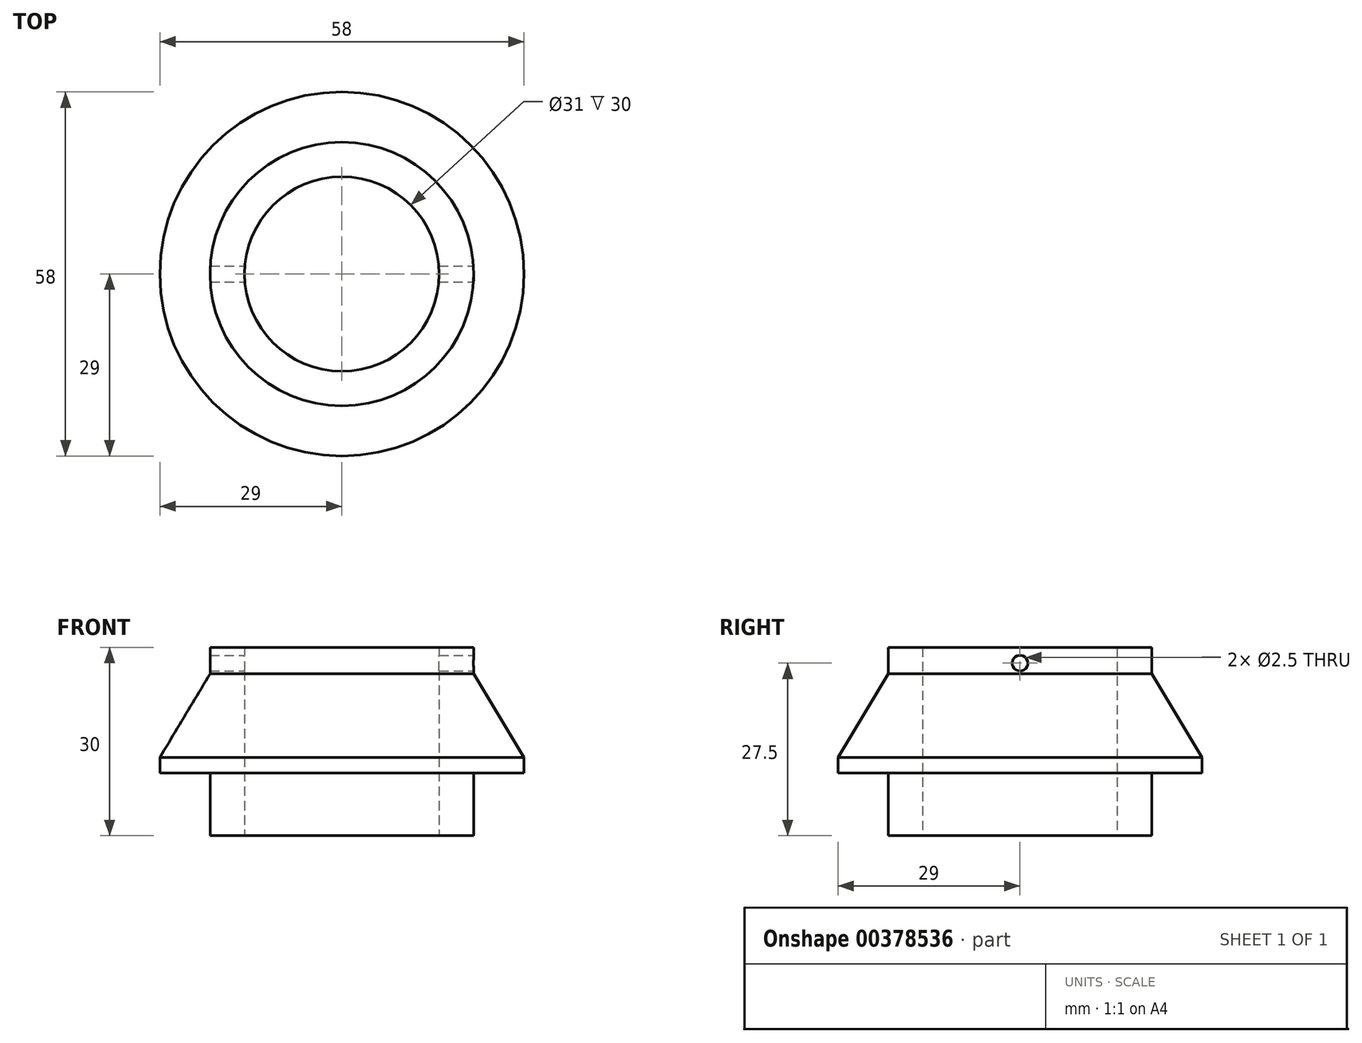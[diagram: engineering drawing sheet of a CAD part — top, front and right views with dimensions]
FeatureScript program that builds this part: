
annotation { "Feature Type Name" : "Feature", "Feature Type Description" : "" }
export const myFeature = defineFeature(function(context is Context, id is Id, definition is map)
    precondition{}
    {
        {
            var Q0;
            Q0=qCreatedBy(makeId("Front.planeOp"),FACE);
            var sketch = newSketch(context, id + "F0", { "sketchPlane" : qUnion([Q0])});
            skLineSegment(sketch, "E0.bottom", {"start": v(15.5, 0) * mm, "end": v(21, 0) * mm});
            skLineSegment(sketch, "E0.top", {"start": v(15.5, 30) * mm, "end": v(21, 30) * mm});
            skLineSegment(sketch, "E0.left", {"start": v(15.5, 0) * mm, "end": v(15.5, 30) * mm});
            skLineSegment(sketch, "E0.right", {"start": v(21, 0) * mm, "end": v(21, 30) * mm});
            skLineSegment(sketch, "E1.bottom", {"start": v(21, 10) * mm, "end": v(29, 10) * mm});
            skLineSegment(sketch, "E1.top", {"start": v(21, 21.2) * mm, "end": v(29, 21.2) * mm});
            skLineSegment(sketch, "E1.left", {"start": v(21, 10) * mm, "end": v(21, 21.2) * mm});
            skLineSegment(sketch, "E1.right", {"start": v(29, 10) * mm, "end": v(29, 21.2) * mm});
            skLineSegment(sketch, "E2", {"start": v(21, 25.8) * mm, "end": v(29, 12.47) * mm});
            skLineSegment(sketch, "E3", {"start": v(0, 0) * mm, "end": v(0, 35.69) * mm});
            skSolve(sketch);
        }
        {
            var Q0;
            {var subQ1=sQuery(id+"F0.wireOp",EDGE,"E1.bottom");Q0=makeQuery(id+"F0.imprint","IMPRINT",FACE,{"disambiguationData":[TD([[makeQuery(id+"F0.imprint","IMPRINT",EDGE,{"derivedFrom":subQ1}),1.0]])]});}
            var Q1;
            {var subQ1=sQuery(id+"F0.wireOp",EDGE,"E0.right");var subQ3=sQuery(id+"F0.wireOp",EDGE,"E2");var subQ4=makeQuery(id+"F0.imprint","INTERSECT",VERTEX,{"derivedFrom":[subQ1,subQ3]});Q1=makeQuery(id+"F0.imprint","IMPRINT",FACE,{"disambiguationData":[TD([[makeQuery(id+"F0.imprint","IMPRINT",EDGE,{"disambiguationData":[TD([[subQ4,-1.0]])],"derivedFrom":subQ3}),-1.0]])]});}
            var Q2;
            {var subQ1=sQuery(id+"F0.wireOp",EDGE,"E0.bottom");Q2=makeQuery(id+"F0.imprint","IMPRINT",FACE,{"disambiguationData":[TD([[makeQuery(id+"F0.imprint","IMPRINT",EDGE,{"derivedFrom":subQ1}),1.0]])]});}
            var Q3;
            Q3=sQuery(id+"F0.wireOp",EDGE,"E3");
            revolve(context, id + "F1", {"entities" : qUnion([Q0, Q1, Q2]), "axis" : qUnion([Q3]), "revolveType" : RevolveType.FULL});
        }
        {
            var Q0;
            Q0=qCreatedBy(makeId("Right.planeOp"),FACE);
            var sketch = newSketch(context, id + "F2", { "sketchPlane" : qUnion([Q0])});
            skCircle(sketch, "E4", {"center": v(0, 27.5) * mm, "radius": 1.25 * mm});
            skSolve(sketch);
        }
        {
            var Q0;
            Q0=makeQuery(id+"F2.imprint","IMPRINT",FACE,{"disambiguationData":[TD([[makeQuery(id+"F2.imprint","IMPRINT",EDGE,{"derivedFrom":sQuery(id+"F2.wireOp",EDGE,"E4")}),1.0]])]});
            extrude(context, id + "F3", {"entities" : qUnion([Q0]), "operationType" : NewBodyOperationType.REMOVE, "endBound" : BoundingType.THROUGH_ALL, "oppositeDirection" : true, "depth" : 25 * mm, "hasSecondDirection" : true, "secondDirectionOppositeDirection" : false, "secondDirectionDepth" : 25 * mm});
        }
    });
